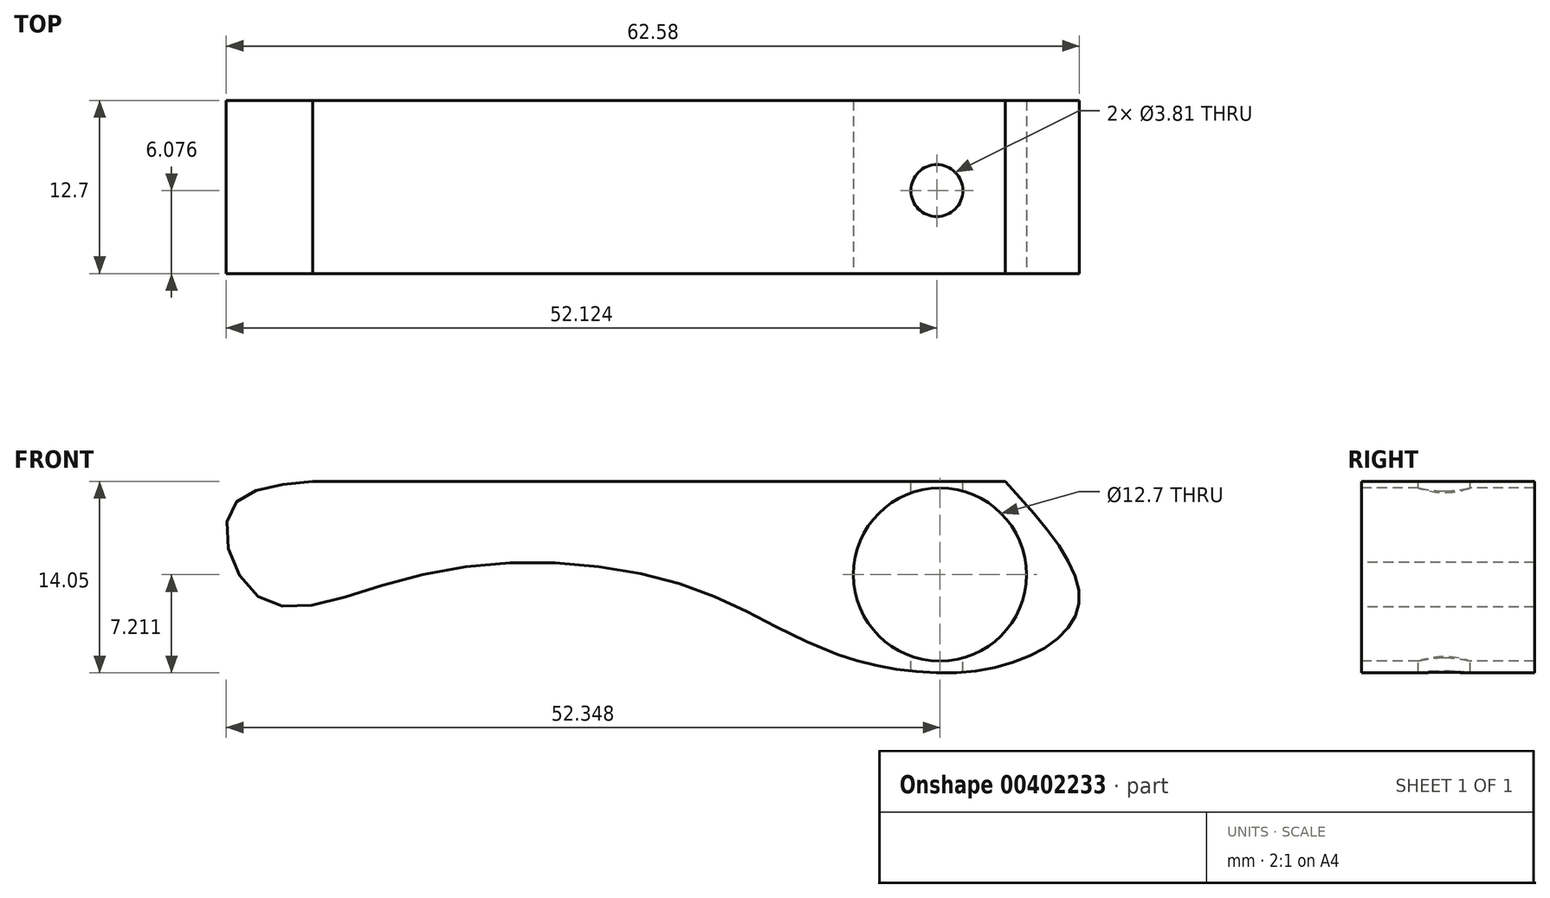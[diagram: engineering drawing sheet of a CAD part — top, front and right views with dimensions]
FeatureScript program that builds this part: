
annotation { "Feature Type Name" : "Feature", "Feature Type Description" : "" }
export const myFeature = defineFeature(function(context is Context, id is Id, definition is map)
    precondition{}
    {
        {
            var Q0;
            Q0=qCreatedBy(makeId("Front.planeOp"),FACE);
            var sketch = newSketch(context, id + "F0", { "sketchPlane" : qUnion([Q0])});
            skLineSegment(sketch, "E0", {"start": v(-38.52, 0) * mm, "end": v(12.28, 0) * mm});
            skLineSegment(sketch, "E1", {"start": v(0, 0) * mm, "end": v(0, -12.7) * mm});
            skFitSpline(sketch, "E2", {"points": [v(12.28, 0) * mm, v(17.7, -8.85) * mm, v(12.28, -13.46) * mm, v(0, -12.7) * mm, v(-11.43, -7.56) * mm, v(-30.42, -6.82) * mm, v(-42.22, -8.66) * mm, v(-44.61, -2.21) * mm, v(-38.52, 0) * mm], "startDerivative": vector(68.58, -76.1) * mm, "endDerivative": vector(81.01, 6.94) * mm});
            skSolve(sketch);
        }
        {
            var Q0;
            Q0=makeQuery(id+"F0.imprint","IMPRINT",FACE,{"disambiguationData":[TD([[makeQuery(id+"F0.imprint","IMPRINT",EDGE,{"derivedFrom":sQuery(id+"F0.wireOp",EDGE,"E0")}),-1.0]])]});
            extrude(context, id + "F1", {"entities" : qUnion([Q0]), "depth" : 12.7 * mm});
        }
        {
            var Q0;
            Q0=qCreatedBy(makeId("Front.planeOp"),FACE);
            cPlane(context, id + "F2", {"entities" : qUnion([Q0]), "cplaneType" : CPlaneType.OFFSET, "offset" : 12.7 * mm, "width" : 152.4 * mm, "height" : 152.4 * mm});
        }
        {
            var Q0;
            Q0=qCreatedBy(id+"F2.planeOp",FACE);
            var sketch = newSketch(context, id + "F3", { "sketchPlane" : qUnion([Q0])});
            skCircle(sketch, "E3", {"center": v(7.48, -6.84) * mm, "radius": 6 * mm});
            skSolve(sketch);
        }
        {
            var Q0;
            Q0=sQuery(id+"F3.wireOp",VERTEX,"E3.center");
            var Q1;
            Q1=makeQuery(id+"F1.opExtrude","SWEPT_BODY",BODY,{"disambiguationData":[OSD([sQuery(id+"F0.wireOp",EDGE,"E0"),sQuery(id+"F0.wireOp",EDGE,"E2")])]});
            hole(context, id + "F4", {"style" : HoleStyle.SIMPLE, "endStyle" : HoleEndStyle.THROUGH, "holeDiameter" : 12.7 * mm, "isTappedThrough" : true, "tappedDepth" : 12.7 * mm, "tapClearance" : 3, "locations" : qUnion([Q0]), "scope" : qUnion([Q1])});
        }
        {
            var Q0;
            Q0=qCreatedBy(makeId("Top.planeOp"),FACE);
            var sketch = newSketch(context, id + "F5", { "sketchPlane" : qUnion([Q0])});
            skCircle(sketch, "E4", {"center": v(7.25, -6.62) * mm, "radius": 1.9 * mm});
            skSolve(sketch);
        }
        {
            var Q0;
            Q0=sQuery(id+"F5.wireOp",VERTEX,"E4.center");
            var Q1;
            Q1=makeQuery(id+"F1.opExtrude","SWEPT_BODY",BODY,{"disambiguationData":[OSD([sQuery(id+"F0.wireOp",EDGE,"E0"),sQuery(id+"F0.wireOp",EDGE,"E2")])]});
            hole(context, id + "F6", {"style" : HoleStyle.SIMPLE, "endStyle" : HoleEndStyle.THROUGH, "holeDiameter" : 3.8 * mm, "isTappedThrough" : true, "tappedDepth" : 12.7 * mm, "tapClearance" : 3, "locations" : qUnion([Q0]), "scope" : qUnion([Q1])});
        }
    });
